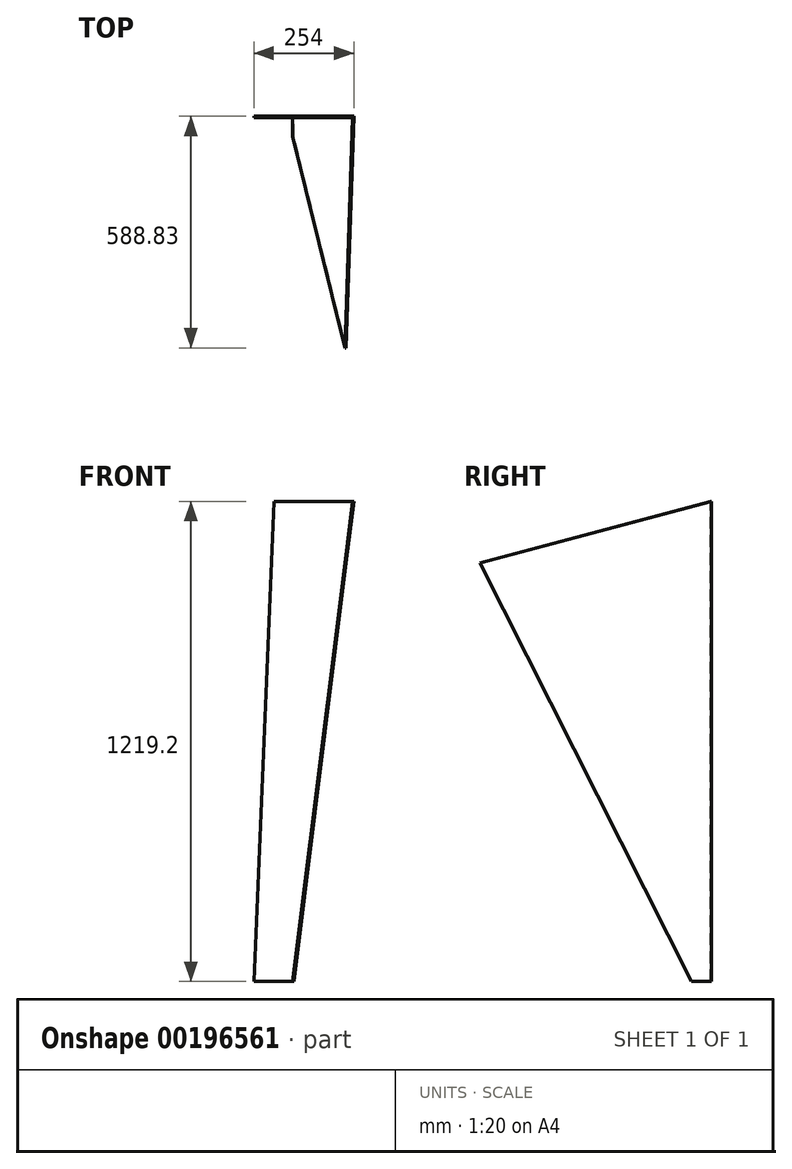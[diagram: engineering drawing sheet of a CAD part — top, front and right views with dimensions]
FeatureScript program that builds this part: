
annotation { "Feature Type Name" : "Feature", "Feature Type Description" : "" }
export const myFeature = defineFeature(function(context is Context, id is Id, definition is map)
    precondition{}
    {
        {
            var Q0;
            Q0=qCreatedBy(makeId("Front.planeOp"),FACE);
            var sketch = newSketch(context, id + "F0", { "sketchPlane" : qUnion([Q0])});
            skLineSegment(sketch, "E0.bottom", {"start": v(203.2, 609.6) * mm, "end": v(-203.2, 609.6) * mm});
            skLineSegment(sketch, "E0.top", {"start": v(50.8, -609.6) * mm, "end": v(-50.8, -609.6) * mm});
            skPoint(sketch, "E0.middle", {"position": v(0, 0) * mm});
            skLineSegment(sketch, "E1", {"start": v(0, 609.6) * mm, "end": v(0, -609.6) * mm});
            skLineSegment(sketch, "E2", {"start": v(-50.8, -609.6) * mm, "end": v(-203.2, 609.6) * mm});
            skLineSegment(sketch, "E3", {"start": v(50.8, -609.6) * mm, "end": v(203.2, 609.6) * mm});
            skPoint(sketch, "E4.orphan", {"position": v(-203.2, -609.6) * mm});
            skPoint(sketch, "E0.left.end.orphan", {"position": v(203.2, -609.6) * mm});
            skSolve(sketch);
        }
        {
            var Q0;
            Q0=makeQuery(id+"F0.imprint","IMPRINT",FACE,{"disambiguationData":[TD([[makeQuery(id+"F0.imprint","IMPRINT",EDGE,{"derivedFrom":sQuery(id+"F0.wireOp",EDGE,"E0.bottom")}),1.0]])]});
            extrude(context, id + "F1", {"entities" : qUnion([Q0]), "depth" : 3.17 * mm});
        }
        {
            var Q0;
            Q0=makeQuery(id+"F1.opExtrude","CAP_FACE",FACE,{"disambiguationData":[OSD([sQuery(id+"F0.wireOp",EDGE,"E0.bottom"),sQuery(id+"F0.wireOp",EDGE,"E0.top"),sQuery(id+"F0.wireOp",EDGE,"E2"),sQuery(id+"F0.wireOp",EDGE,"E3")])],"isStart":false});
            var sketch = newSketch(context, id + "F2", { "sketchPlane" : qUnion([Q0])});
            skLineSegment(sketch, "E5", {"start": v(-203.2, 609.6) * mm, "end": v(-50.8, -609.6) * mm});
            skLineSegment(sketch, "E6.0", {"start": v(-200.05, 610) * mm, "end": v(-47.65, -609.2) * mm});
            skLineSegment(sketch, "E7", {"start": v(-200.05, 610) * mm, "end": v(-203.2, 609.6) * mm});
            skLineSegment(sketch, "E8", {"start": v(-47.65, -609.2) * mm, "end": v(-50.8, -609.6) * mm});
            skLineSegment(sketch, "E9.MirrorCS", {"start": v(200.05, 610) * mm, "end": v(47.65, -609.2) * mm});
            skLineSegment(sketch, "E10.MirrorCS", {"start": v(200.05, 610) * mm, "end": v(203.2, 609.6) * mm});
            skLineSegment(sketch, "E11.MirrorCS", {"start": v(203.2, 609.6) * mm, "end": v(50.8, -609.6) * mm});
            skLineSegment(sketch, "E12.MirrorCS", {"start": v(47.65, -609.2) * mm, "end": v(50.8, -609.6) * mm});
            skSolve(sketch);
        }
        {
            var Q0;
            {var subQ4=sQuery(id+"F2.wireOp",EDGE,"E11.MirrorCS");Q0=makeQuery(id+"F2.imprint","IMPRINT",FACE,{"disambiguationData":[TD([[makeQuery(id+"F2.imprint","IMPRINT",EDGE,{"derivedFrom":subQ4}),1.0]])]});}
            extrude(context, id + "F3", {"entities" : qUnion([Q0]), "operationType" : NewBodyOperationType.ADD, "depth" : 609.6 * mm});
        }
        {
            var Q0;
            Q0=makeQuery(id+"F3.boolean.opBoolean","MERGE",FACE,{"derivedFrom":[makeQuery(id+"F1.opExtrude","SWEPT_FACE",FACE,{"disambiguationData":[OSD([sQuery(id+"F0.wireOp",EDGE,"E3")])]}),makeQuery(id+"F3.opExtrude","SWEPT_FACE",FACE,{"disambiguationData":[OSD([sQuery(id+"F2.wireOp",EDGE,"E11.MirrorCS")])]})]});
            var sketch = newSketch(context, id + "F4", { "sketchPlane" : qUnion([Q0])});
            skLineSegment(sketch, "E13", {"start": v(-612.78, -598.6) * mm, "end": v(-561.98, -598.6) * mm});
            skLineSegment(sketch, "E14", {"start": v(0, 630.1) * mm, "end": v(-588.83, 472.32) * mm});
            skLineSegment(sketch, "E15", {"start": v(-588.83, 472.32) * mm, "end": v(-50.8, -598.6) * mm});
            skLineSegment(sketch, "E16", {"start": v(-50.8, -598.6) * mm, "end": v(-50.8, -900.09) * mm});
            skLineSegment(sketch, "E17", {"start": v(-50.8, -900.09) * mm, "end": v(-712.45, -900.09) * mm});
            skLineSegment(sketch, "E18", {"start": v(-712.45, -900.09) * mm, "end": v(-712.45, 731.37) * mm});
            skLineSegment(sketch, "E19", {"start": v(-712.45, 731.37) * mm, "end": v(0, 731.37) * mm});
            skLineSegment(sketch, "E20", {"start": v(0, 731.37) * mm, "end": v(0, 630.1) * mm});
            skLineSegment(sketch, "E21", {"start": v(-588.83, 472.32) * mm, "end": v(0, 630.1) * mm});
            skSolve(sketch);
        }
        {
            var Q0;
            Q0=qSketchRegion(id+"F4",true);
            extrude(context, id + "F5", {"entities" : qUnion([Q0]), "operationType" : NewBodyOperationType.REMOVE, "oppositeDirection" : true, "depth" : 1211.58 * mm});
        }
        {
            var Q0;
            Q0=makeQuery(id+"F1.opExtrude","CAP_FACE",FACE,{"disambiguationData":[OSD([sQuery(id+"F0.wireOp",EDGE,"E0.bottom"),sQuery(id+"F0.wireOp",EDGE,"E0.top"),sQuery(id+"F0.wireOp",EDGE,"E2"),sQuery(id+"F0.wireOp",EDGE,"E3")])],"isStart":false});
            var sketch = newSketch(context, id + "F6", { "sketchPlane" : qUnion([Q0])});
            skLineSegment(sketch, "E22", {"start": v(-50.8, -609.6) * mm, "end": v(0, 609.6) * mm});
            skPoint(sketch, "E22.endSnap0", {"position": v(-3.43, 609.6) * mm});
            skSolve(sketch);
        }
        {
            var Q0;
            {var subQ0=sQuery(id+"F6.wireOp",EDGE,"E22");Q0=makeQuery(id+"F6.imprint","IMPRINT",FACE,{"disambiguationData":[TD([[makeQuery(id+"F6.imprint","IMPRINT",EDGE,{"derivedFrom":subQ0}),1.0]])]});}
            extrude(context, id + "F7", {"entities" : qUnion([Q0]), "operationType" : NewBodyOperationType.REMOVE, "oppositeDirection" : true, "depth" : 25.4 * mm});
        }
    });
